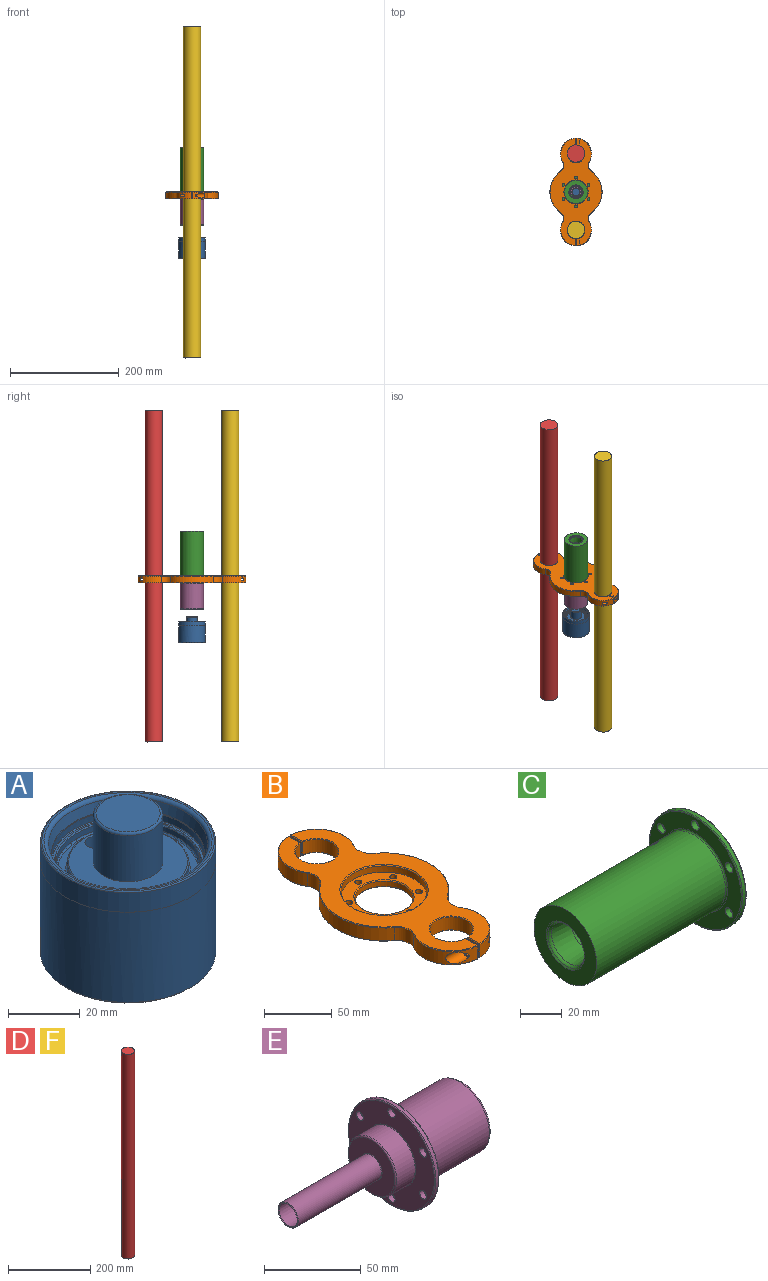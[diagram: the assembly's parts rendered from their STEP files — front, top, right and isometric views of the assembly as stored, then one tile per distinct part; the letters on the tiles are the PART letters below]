
ASSEMBLY  parts=6 mates=6
PART A: 32 faces, bbox 52.9x52.9x48 mm
  f0: cylinder r=12.26mm len=24.51mm, axis (0,0,1), area 1173.5mm2, adj f27,f28
  f1: cylinder r=24.43mm len=48.87mm, axis (0,0,-1), area 4729.7mm2, adj f2,f16,f25
  f2: cone r=23.8mm half-angle=45deg, axis (0,0,1), area 136.1mm2, adj f1,f28
  f3: torus R=17.4mm, axis (0,0,1), area 77.2mm2, adj f12,f26
  f4: torus R=19.61mm, axis (0,0,1), area 99.9mm2, adj f14,f26
  f5: cylinder r=24.43mm len=48.87mm, axis (0,0,-1), area 1020.7mm2, adj f6,f25
  f6: torus R=24.05mm, axis (0,0,1), area 91.4mm2, adj f5,f24
  f7: torus R=23.44mm, axis (0,0,1), area 241.7mm2, adj f8,f24
  f8: cone r=21.81mm half-angle=13.6deg, axis (0,0,1), area 462.8mm2, adj f7,f9
  f9: torus R=22.64mm, axis (0,0,1), area 40.4mm2, adj f8,f10
  f10: cylinder r=21.37mm len=42.75mm, axis (0,0,-1), area 298.4mm2, adj f9,f11
  f11: torus R=21.12mm, axis (0,0,1), area 53.4mm2, adj f10,f22
  f12: cylinder r=16.94mm len=33.88mm, axis (0,0,1), area 197.4mm2, adj f3,f13
  f13: torus R=16.56mm, axis (0,0,1), area 63.2mm2, adj f12,f23
  f14: cylinder r=20.12mm len=40.24mm, axis (0,0,1), area 228mm2, adj f4,f15
  f15: torus R=20.5mm, axis (0,0,1), area 76.2mm2, adj f14,f22
  f16: cylinder r=4.17mm len=11.01mm, axis (0,1,0), area 274.5mm2, adj f1,f17,f18,f19,f20,f21
  f17: cylinder r=2.78mm len=13.62mm, axis (0,0,1), area 173.9mm2, adj f16,f18,f19,f20,f23
  f18: plane 5.56x5.36mm, normal (0,0,1), area 18.7mm2, adj f16,f17,f21
  f19: plane 6.21x1.39mm, normal (0,1,0), area 6mm2, adj f16,f17
  f20: plane 6.21x1.39mm, normal (0,1,0), area 6mm2, adj f16,f17
  f21: plane 2.05x0.13mm, normal (0,1,0), area 0.2mm2, adj f16,f18
  f22: plane 42.24x42.24mm, normal (0,0,1), area 81.1mm2, adj f11,f15
  f23: plane 33.12x33.12mm, normal (0,0,1), area 541.2mm2, adj f13,f17,f29
  f24: plane 48.11x48.11mm, normal (0,0,1), area 91.9mm2, adj f6,f7
  f25: plane 48.87x48.87mm, normal (0,0,1), area 0.1mm2, adj f1,f5
  f26: plane 39.22x39.22mm, normal (0,0,1), area 257.2mm2, adj f3,f4
  f27: plane 24.51x24.51mm, normal (0,0,-1), area 471.9mm2, adj f0
  f28: plane 47.6x47.6mm, normal (0,0,-1), area 1307.6mm2, adj f0,f2
  f29: cylinder r=9.71mm len=19.42mm, axis (0,0,-1), area 960.8mm2, adj f23,f31
  f30: plane 17.9x17.9mm, normal (0,0,1), area 251.5mm2, adj f31
  f31: torus R=8.95mm, axis (0,0,1), area 70.9mm2, adj f29,f30
PART B: 78 faces, bbox 95.8x197.4x12.7 mm
  f0: cylinder r=5.04mm len=17.1mm, axis (1,0,0), area 315.8mm2, adj f29,f77
  f1: cylinder r=3.3mm len=6.6mm, axis (1,0,0), area 105.4mm2, adj f72,f77
  f2: cylinder r=2.71mm len=20.22mm, axis (-1,0,0), area 285.1mm2, adj f37,f69
  f3: cylinder r=15.88mm len=31.75mm, axis (0,0,1), area 1138.1mm2, adj f4,f5,f68,f71
  f4: cone r=16.13mm half-angle=45deg, axis (0,0,-1), area 71.3mm2, adj f3,f68,f71,f73,f74,f75
  f5: cone r=16.13mm half-angle=45deg, axis (0,0,1), area 71.3mm2, adj f3,f67,f68,f70,f71,f76
  f6: cylinder r=5.04mm len=17.1mm, axis (-1,0,0), area 315.8mm2, adj f31,f66
  f7: cylinder r=3.3mm len=6.6mm, axis (-1,0,0), area 105.4mm2, adj f63,f66
  f8: cylinder r=2.71mm len=20.22mm, axis (1,0,0), area 285.1mm2, adj f35,f60
  f9: cylinder r=15.88mm len=31.75mm, axis (0,0,-1), area 1138.1mm2, adj f10,f11,f58,f62
  f10: cone r=16.13mm half-angle=45deg, axis (0,0,-1), area 71.3mm2, adj f9,f58,f62,f64,f65,f75
  f11: cone r=16.13mm half-angle=45deg, axis (0,0,1), area 71.3mm2, adj f9,f58,f59,f61,f62,f67
  f12: cylinder r=2.6mm len=6.35mm, axis (0,0,1), area 103.9mm2, adj f57,f75
  f13: cylinder r=2.6mm len=6.35mm, axis (0,0,1), area 103.9mm2, adj f57,f75
  f14: cylinder r=2.6mm len=6.35mm, axis (0,0,1), area 103.9mm2, adj f57,f75
  f15: cylinder r=2.6mm len=6.35mm, axis (0,0,1), area 103.9mm2, adj f57,f75
  f16: cylinder r=2.6mm len=6.35mm, axis (0,0,1), area 103.9mm2, adj f57,f75
  f17: cylinder r=2.6mm len=6.35mm, axis (0,0,1), area 103.9mm2, adj f57,f75
  f18: cone r=21.83mm half-angle=45deg, axis (0,0,-1), area 147.8mm2, adj f20,f75
  f19: cone r=32.18mm half-angle=45deg, axis (0,0,1), area 217.9mm2, adj f21,f67
  f20: cylinder r=21.45mm len=42.91mm, axis (0,0,1), area 650.5mm2, adj f18,f22
  f21: cylinder r=31.8mm len=63.6mm, axis (0,0,1), area 1116.5mm2, adj f19,f57
  f22: cone r=21.83mm half-angle=45deg, axis (0,0,1), area 147.8mm2, adj f20,f57
  f23: cone r=28.32mm half-angle=45deg, axis (0,0,1), area 42.1mm2, adj f37,f43,f56,f74,f75
  f24: cone r=47.67mm half-angle=45deg, axis (0,0,1), area 64.7mm2, adj f36,f55,f56,f75
  f25: cone r=28.32mm half-angle=45deg, axis (0,0,1), area 42.1mm2, adj f35,f46,f55,f65,f75
  f26: cone r=28.32mm half-angle=45deg, axis (0,0,1), area 42.1mm2, adj f31,f49,f54,f64,f75
  f27: cone r=28.32mm half-angle=45deg, axis (0,0,1), area 42.1mm2, adj f29,f52,f53,f73,f75
  f28: cone r=47.67mm half-angle=45deg, axis (0,0,1), area 64.7mm2, adj f30,f53,f54,f75
  f29: cylinder r=28.57mm len=43.1mm, axis (0,0,1), area 689.2mm2, adj f0,f27,f33,f51,f52
  f30: cylinder r=47.92mm len=77.67mm, axis (0,0,1), area 1058mm2, adj f28,f34,f50,f51
  f31: cylinder r=28.57mm len=43.1mm, axis (0,0,-1), area 689.2mm2, adj f6,f26,f32,f49,f50
  f32: cone r=28.32mm half-angle=45deg, axis (0,0,-1), area 42.1mm2, adj f31,f48,f49,f61,f67
  f33: cone r=28.32mm half-angle=45deg, axis (0,0,-1), area 42.1mm2, adj f29,f47,f52,f67,f76
  f34: cone r=47.67mm half-angle=45deg, axis (0,0,-1), area 64.7mm2, adj f30,f47,f48,f67
  f35: cylinder r=28.57mm len=43.1mm, axis (0,0,-1), area 689.2mm2, adj f8,f25,f39,f45,f46
  f36: cylinder r=47.92mm len=77.67mm, axis (0,0,1), area 1058mm2, adj f24,f40,f44,f45
  f37: cylinder r=28.57mm len=43.1mm, axis (0,0,1), area 689.2mm2, adj f2,f23,f38,f43,f44
  f38: cone r=28.32mm half-angle=45deg, axis (0,0,-1), area 42.1mm2, adj f37,f42,f43,f67,f70
  f39: cone r=28.32mm half-angle=45deg, axis (0,0,-1), area 42.1mm2, adj f35,f41,f46,f59,f67
  f40: cone r=47.67mm half-angle=45deg, axis (0,0,-1), area 64.7mm2, adj f36,f41,f42,f67
  f41: cone r=12.95mm half-angle=45deg, axis (0,0,1), area 13.8mm2, adj f39,f40,f45,f67
  f42: cone r=12.95mm half-angle=45deg, axis (0,0,1), area 13.8mm2, adj f38,f40,f44,f67
  f43: plane 12.19x0.51mm, normal (-0.7,0.72,0), area 8.4mm2, adj f23,f37,f38,f69,f70,f74
  f44: cylinder r=12.7mm len=16.76mm, axis (0,0,1), area 219.5mm2, adj f36,f37,f42,f56
  f45: cylinder r=12.7mm len=16.76mm, axis (0,0,-1), area 219.5mm2, adj f35,f36,f41,f55
  f46: plane 12.19x0.51mm, normal (-0.7,-0.72,0), area 8.4mm2, adj f25,f35,f39,f59,f60,f65
  f47: cone r=12.95mm half-angle=45deg, axis (0,0,1), area 13.8mm2, adj f33,f34,f51,f67
  f48: cone r=12.95mm half-angle=45deg, axis (0,0,1), area 13.8mm2, adj f32,f34,f50,f67
  f49: plane 12.19x0.51mm, normal (0.7,-0.72,0), area 8.4mm2, adj f26,f31,f32,f61,f63,f64
  f50: cylinder r=12.7mm len=16.76mm, axis (0,0,1), area 219.5mm2, adj f30,f31,f48,f54
  f51: cylinder r=12.7mm len=16.76mm, axis (0,0,1), area 219.5mm2, adj f29,f30,f47,f53
  f52: plane 12.19x0.51mm, normal (0.7,0.72,0), area 8.4mm2, adj f27,f29,f33,f72,f73,f76
  f53: cone r=12.95mm half-angle=45deg, axis (0,0,-1), area 13.8mm2, adj f27,f28,f51,f75
  f54: cone r=12.95mm half-angle=45deg, axis (0,0,-1), area 13.8mm2, adj f26,f28,f50,f75
  f55: cone r=12.95mm half-angle=45deg, axis (0,0,-1), area 13.8mm2, adj f24,f25,f45,f75
  f56: cone r=12.95mm half-angle=45deg, axis (0,0,-1), area 13.8mm2, adj f23,f24,f44,f75
  f57: plane 63.6x63.6mm, normal (0,0,1), area 1498.9mm2, adj f12,f13,f14,f15,f16,f17,f21,f22
  f58: plane 12.19x0.54mm, normal (-0.73,0.69,0), area 8.8mm2, adj f9,f10,f11,f59,f60,f65
  f59: plane 12.21x0.51mm, normal (-0.71,0,0.71), area 8.6mm2, adj f11,f39,f46,f58,f60,f67
  f60: plane 11.69x11.68mm, normal (-1,0,0), area 113.6mm2, adj f8,f46,f58,f59,f65
  f61: plane 12.21x0.51mm, normal (0.71,0,0.71), area 8.6mm2, adj f11,f32,f49,f62,f63,f67
  f62: plane 12.19x0.54mm, normal (0.73,0.69,0), area 8.8mm2, adj f9,f10,f11,f61,f63,f64
  f63: plane 11.69x11.68mm, normal (1,0,0), area 102.3mm2, adj f7,f49,f61,f62,f64
  f64: plane 12.21x0.51mm, normal (0.71,0,-0.71), area 8.6mm2, adj f10,f26,f49,f62,f63,f75
  f65: plane 12.21x0.51mm, normal (-0.71,0,-0.71), area 8.6mm2, adj f10,f25,f46,f58,f60,f75
  f66: plane 10.08x10.08mm, normal (-1,0,0), area 45.6mm2, adj f6,f7
  f67: plane 196.37x94.83mm, normal (0,0,1), area 6959.7mm2, adj f5,f11,f19,f32,f33,f34,f38,f39
  f68: plane 12.19x0.54mm, normal (-0.73,-0.69,0), area 8.8mm2, adj f3,f4,f5,f69,f70,f74
  f69: plane 11.69x11.68mm, normal (-1,0,0), area 113.6mm2, adj f2,f43,f68,f70,f74
  f70: plane 12.21x0.51mm, normal (-0.71,0,0.71), area 8.6mm2, adj f5,f38,f43,f67,f68,f69
  f71: plane 12.19x0.54mm, normal (0.73,-0.69,0), area 8.8mm2, adj f3,f4,f5,f72,f73,f76
  f72: plane 11.69x11.68mm, normal (1,0,0), area 102.3mm2, adj f1,f52,f71,f73,f76
  f73: plane 12.21x0.51mm, normal (0.71,0,-0.71), area 8.6mm2, adj f4,f27,f52,f71,f72,f75
  f74: plane 12.21x0.51mm, normal (-0.71,0,-0.71), area 8.6mm2, adj f4,f23,f43,f68,f69,f75
  f75: plane 196.37x94.83mm, normal (0,0,-1), area 8612.6mm2, adj f4,f10,f12,f13,f14,f15,f16,f17
  f76: plane 12.21x0.51mm, normal (0.71,0,0.71), area 8.6mm2, adj f5,f33,f52,f67,f71,f72
  f77: plane 10.08x10.08mm, normal (-1,0,0), area 45.6mm2, adj f0,f1
PART C: 27 faces, bbox 92.5x68.8x68.8 mm
  f0: cone r=10.99mm half-angle=5.4deg, axis (-1,0,0), area 867.4mm2, adj f2,f24
  f1: cone r=12.33mm half-angle=47.7deg, axis (-1,0,0), area 71.5mm2, adj f2,f7
  f2: torus R=14.07mm, axis (1,0,0), area 139.5mm2, adj f0,f1
  f3: cylinder r=21.33mm len=87.72mm, axis (1,0,0), area 11740.6mm2, adj f4,f5,f7,f9
  f4: bspline ~4.52x2.42mm, area 4.6mm2, adj f3,f5,f6
  f5: bspline ~4.52x2.36mm, area 4.6mm2, adj f3,f4,f6
  f6: cylinder r=1.73mm len=10.72mm, axis (0,-0.59,-0.81), area 115.4mm2, adj f4,f5,f23
  f7: plane 42.66x42.66mm, normal (-1,0,0), area 897mm2, adj f1,f3
  f8: plane 34.43x34.43mm, normal (1,0,0), area 568.9mm2, adj f13,f22
  f9: torus R=22.09mm, axis (-1,0,0), area 162.6mm2, adj f3,f26
  f10: torus R=31.25mm, axis (-1,0,0), area 158.3mm2, adj f11,f26
  f11: cylinder r=31.76mm len=63.52mm, axis (1,0,0), area 430.9mm2, adj f10,f12
  f12: torus R=31.25mm, axis (-1,0,0), area 158.3mm2, adj f11,f25
  f13: torus R=17.21mm, axis (-1,0,0), area 65.7mm2, adj f8,f14
  f14: cylinder r=17.59mm len=35.19mm, axis (1,0,0), area 1516.6mm2, adj f13,f15
  f15: torus R=18.1mm, axis (-1,0,0), area 89.2mm2, adj f14,f25
  f16: cylinder r=2.6mm len=5.21mm, axis (-1,0,0), area 52mm2, adj f25,f26
  f17: cylinder r=2.6mm len=5.21mm, axis (-1,0,0), area 52mm2, adj f25,f26
  f18: cylinder r=2.6mm len=5.21mm, axis (-1,0,0), area 52mm2, adj f25,f26
  f19: cylinder r=2.6mm len=5.21mm, axis (-1,0,0), area 52mm2, adj f25,f26
  f20: cylinder r=2.6mm len=5.21mm, axis (-1,0,0), area 52mm2, adj f25,f26
  f21: cylinder r=2.6mm len=5.21mm, axis (-1,0,0), area 52mm2, adj f25,f26
  f22: torus R=10.73mm, axis (1,0,0), area 52.2mm2, adj f8,f23
  f23: cylinder r=10.23mm len=59.32mm, axis (-1,0,0), area 3804.7mm2, adj f6,f22,f24
  f24: torus R=35.63mm, axis (1,0,0), area 155.6mm2, adj f0,f23
  f25: plane 62.5x62.5mm, normal (1,0,0), area 1910.7mm2, adj f12,f15,f16,f17,f18,f19,f20,f21
  f26: plane 62.5x62.5mm, normal (-1,0,0), area 1406.6mm2, adj f9,f10,f16,f17,f18,f19,f20,f21
PART D: 3 faces, bbox 31.8x31.8x609.6 mm
  f0: cylinder r=15.88mm len=609.6mm, axis (0,0,-1), area 60804.9mm2, adj f1,f2
  f1: plane 31.75x31.75mm, normal (0,0,1), area 791.7mm2, adj f0
  f2: plane 31.75x31.75mm, normal (0,0,-1), area 791.7mm2, adj f0
PART E: 32 faces, bbox 126.9x68.7x68.7 mm
  f0: torus R=16.75mm, axis (-1,0,0), area 129.7mm2, adj f18,f23
  f1: revolved ~18.37x18.37mm, area 354.5mm2, adj f17,f24
  f2: cone r=11.85mm half-angle=9deg, axis (1,0,0), area 2239.3mm2, adj f3,f10
  f3: torus R=16.71mm, axis (1,0,0), area 342.8mm2, adj f2,f22
  f4: torus R=19.96mm, axis (1,0,0), area 260.3mm2, adj f5,f22
  f5: cylinder r=21.23mm len=46.67mm, axis (-1,0,0), area 6224.5mm2, adj f4,f6
  f6: torus R=21.48mm, axis (1,0,0), area 53.4mm2, adj f5,f21
  f7: torus R=31.24mm, axis (1,0,0), area 158.3mm2, adj f8,f21
  f8: cylinder r=31.75mm len=63.5mm, axis (-1,0,0), area 430.7mm2, adj f7,f9
  f9: torus R=31.24mm, axis (1,0,0), area 158.3mm2, adj f8,f20
  f10: torus R=34.59mm, axis (1,0,0), area 232.7mm2, adj f2,f17
  f11: cylinder r=2.6mm len=5.21mm, axis (1,0,0), area 51.9mm2, adj f20,f21
  f12: cylinder r=2.6mm len=5.21mm, axis (1,0,0), area 51.9mm2, adj f20,f21
  f13: cylinder r=2.6mm len=5.21mm, axis (1,0,0), area 51.9mm2, adj f20,f21
  f14: cylinder r=2.6mm len=5.21mm, axis (1,0,0), area 51.9mm2, adj f20,f21
  f15: cylinder r=2.6mm len=5.21mm, axis (1,0,0), area 51.9mm2, adj f20,f21
  f16: cylinder r=2.6mm len=5.21mm, axis (1,0,0), area 51.9mm2, adj f20,f21
  f17: cylinder r=9.19mm len=18.37mm, axis (-1,0,0), area 897.6mm2, adj f1,f10
  f18: cylinder r=17.52mm len=35.03mm, axis (1,0,0), area 1477.8mm2, adj f0,f19
  f19: torus R=17.77mm, axis (-1,0,0), area 44.1mm2, adj f18,f20
  f20: plane 62.48x62.48mm, normal (-1,0,0), area 1946.6mm2, adj f9,f11,f12,f13,f14,f15,f16,f19
  f21: plane 62.48x62.48mm, normal (1,0,0), area 1489.1mm2, adj f6,f7,f11,f12,f13,f14,f15,f16
  f22: plane 39.91x39.91mm, normal (1,0,0), area 374.1mm2, adj f3,f4
  f23: plane 33.51x33.51mm, normal (-1,0,0), area 699.4mm2, adj f0,f31
  f24: cone r=8.16mm half-angle=14.5deg, axis (1,0,0), area 90mm2, adj f1,f25
  f25: cone r=7.75mm half-angle=14.8deg, axis (1,0,0), area 69.8mm2, adj f24,f26
  f26: torus R=32.13mm, axis (-1,0,0), area 288.7mm2, adj f25,f27
  f27: cone r=6.72mm half-angle=0deg, axis (1,0,0), area 2508.4mm2, adj f26,f28
  f28: torus R=6.99mm, axis (-1,0,0), area 24.9mm2, adj f27,f29
  f29: torus R=7.11mm, axis (-1,0,0), area 18.2mm2, adj f28,f30
  f30: cylinder r=7.37mm len=60.57mm, axis (1,0,0), area 2803.5mm2, adj f29,f31
  f31: torus R=7.62mm, axis (-1,0,0), area 18.7mm2, adj f23,f30
PART F: same geometry as D
PLACE A t=(0,0,-83.31)mm
PLACE B rot(axis=(0,-1,0),180deg) t=(0,0,6.35)mm fixed
PLACE C rot(axis=(0,1,0),90deg) t=(0,0,-3.18)mm
PLACE D t=(0,70.14,6.35)mm
PLACE E rot(axis=(0.71,0,-0.71),180deg) t=(0,0,72.45)mm
PLACE F t=(0,-70.14,6.35)mm
MATE fastened C.f1 <-> B.f19  axis (0,0,1) through (0,0,0)mm
MATE slider F.f0 <-> B.f10  axis (0,0,-1) through (0,-70.14,-298.45)mm
MATE fastened E.f2 <-> C.f1  axis (0,0,1) through (0,0,-3.18)mm
MATE slider E.f26 <-> A.f0  axis (0,0,-1) through (0,0,-54.55)mm
MATE planar F.f0 <-> D.f0  axis (0,0,-1) through (0,-70.14,-298.45)mm
MATE slider D.f0 <-> B.f4  axis (0,0,-1) through (0,70.14,-298.45)mm
